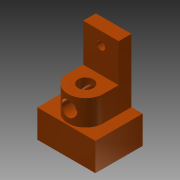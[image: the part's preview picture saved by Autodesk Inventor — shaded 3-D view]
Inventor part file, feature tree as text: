
AUTODESK INVENTOR PART (.ipt)
format: ipt  version: 2013 (Build 170138000, 138)  size: 271,360 bytes
history: native  units: mm
features: extrude x11, sketch x10, fillet x1
ambient origin geometry x8: Origin, YZ Plane, XZ Plane, XY Plane, X Axis, Y Axis, Z Axis, Center Point
bodies: Solid1 (feature_tree)
feature tree (22):
  extrude  "Extrusion1"  Depth=25.0mm TaperAngle=0.0deg
  extrude  "Extrusion2"  Depth=4.62mm
  extrude  "Extrusion3"  Depth=11.0mm TaperAngle=0.0deg
  extrude  "Extrusion4"  Depth=11.0mm TaperAngle=0.0deg
  extrude  "Extrusion5"  Depth=15.0mm
  extrude  "Extrusion6"  Depth=5.0mm
  extrude  "Extrusion11"  Depth=3.2mm
  extrude  "Extrusion7"  Depth=6.0mm
  extrude  "Extrusion8"  Depth=15.266mm
  extrude  "Extrusion9"  Depth=2.0mm
  extrude  "Extrusion10"  Depth=10.0mm TaperAngle=0.0deg
  fillet  "Fillet3"  Radius=10.3mm
  sketch  "Sketch1"  dims[d0=14.0mm d1=25.0mm d2=0.0mm]
  sketch  "Sketch2"  dims[d4=11.43mm d5=4.62mm]
  sketch  "Sketch3"  dims[d6=11.0mm d7=0.0mm d10=11.0mm d11=0.0mm]
  sketch  "Sketch4"  dims[d12=11.0mm d13=-7.853982mm d16=11.0mm d17=0.0mm]
  sketch  "Sketch5"  dims[d18=11.0mm d19=0.0mm d21=15.0mm]
  sketch  "Sketch6"  dims[d22=11.0mm d23=0.0mm d24=5.0mm]
  sketch  "Sketch7"  dims[d25=5.0mm d26=3.2mm]
  sketch  "Sketch8"  dims[d27=5.0mm d28=0.0mm d29=6.0mm]
  sketch  "Sketch9"  dims[d31=11.0mm d32=0.0mm d33=15.266mm]
  sketch  "Sketch11"  dims[d35=7.633mm d37=2.0mm d38=10.0mm d39=0.0mm d44=10.3mm d46=3.0mm d47=6.0mm d49=10.0mm d50=0.0mm d51=5.0mm d52=16.0mm d53=2.0mm d54=5.0mm]
